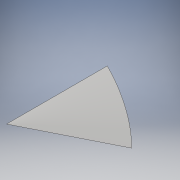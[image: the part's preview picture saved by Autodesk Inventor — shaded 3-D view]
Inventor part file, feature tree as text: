
AUTODESK INVENTOR PART (.ipt)
format: ipt  version: 2018 (Build 220112000, 112)  size: 96,256 bytes
history: native  units: mm
features: revolve x1, sketch x1
ambient origin geometry x8: Origin, YZ Plane, XZ Plane, XY Plane, X Axis, Y Axis, Z Axis, Center Point
bodies: Volumenkörper1 (feature_tree)
feature tree (2):
  revolve  "Umdrehung1"
  sketch  "Skizze1"  dims[d4=40.0mm d5=40.0mm d7=45.0deg]
